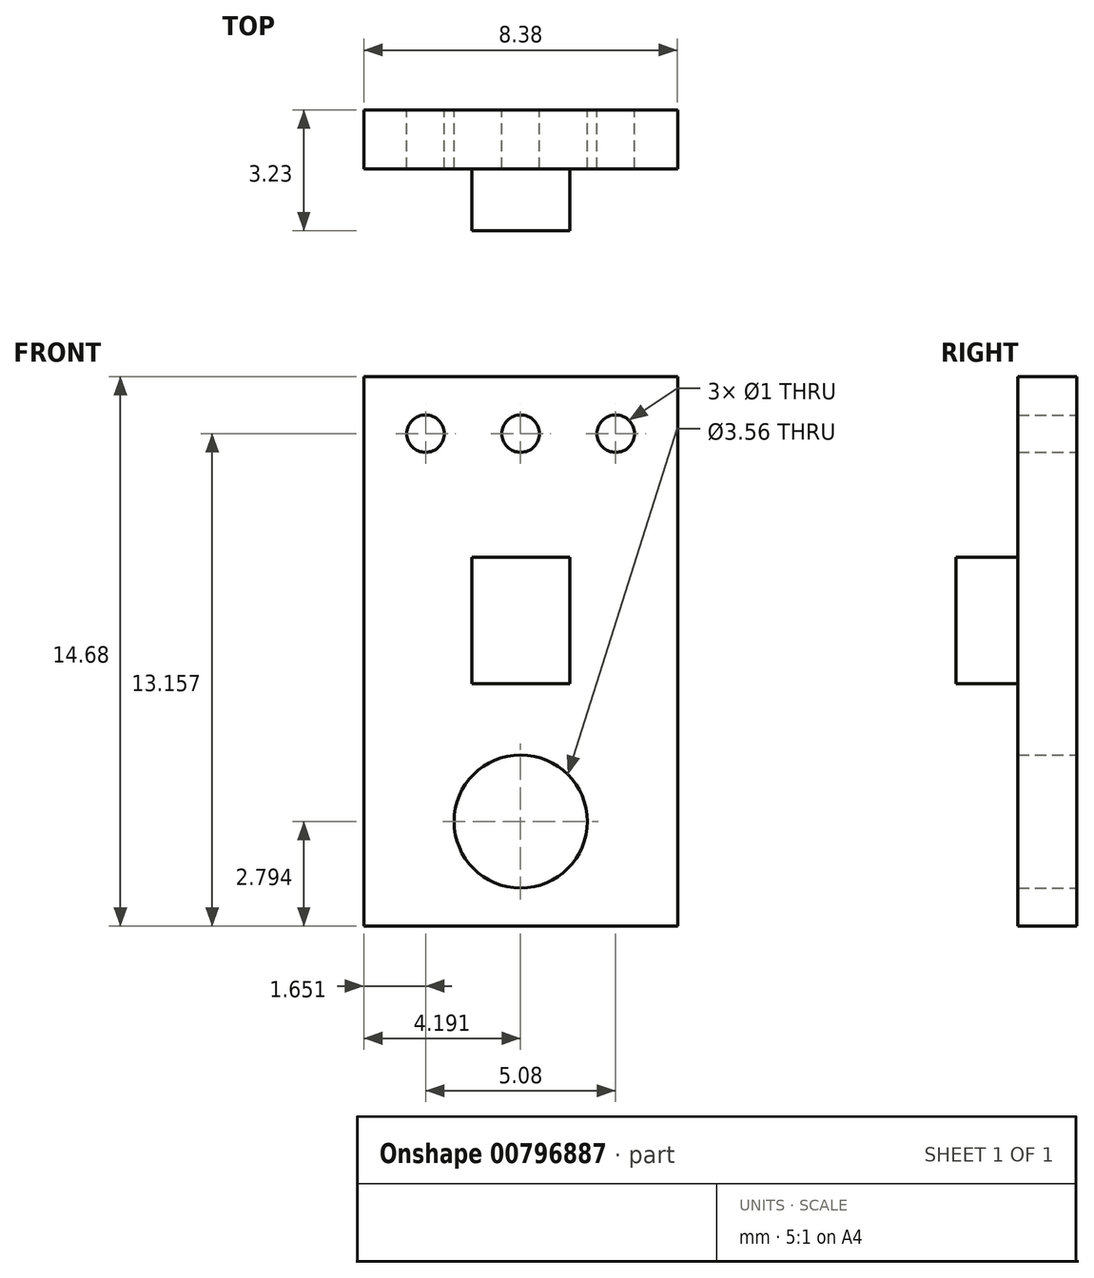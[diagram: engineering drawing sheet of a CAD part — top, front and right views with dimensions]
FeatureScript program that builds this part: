
annotation { "Feature Type Name" : "Feature", "Feature Type Description" : "" }
export const myFeature = defineFeature(function(context is Context, id is Id, definition is map)
    precondition{}
    {
        {
            var Q0;
            Q0=qCreatedBy(makeId("Front.planeOp"),FACE);
            var sketch = newSketch(context, id + "F0", { "sketchPlane" : qUnion([Q0])});
            skLineSegment(sketch, "E0.bottom", {"start": v(0, 0) * mm, "end": v(8.38, 0) * mm});
            skLineSegment(sketch, "E0.top", {"start": v(0, 14.68) * mm, "end": v(8.38, 14.68) * mm});
            skLineSegment(sketch, "E0.left", {"start": v(0, 0) * mm, "end": v(0, 14.68) * mm});
            skLineSegment(sketch, "E0.right", {"start": v(8.38, 0) * mm, "end": v(8.38, 14.68) * mm});
            skCircle(sketch, "E1", {"center": v(4.2, 2.8) * mm, "radius": 1.78 * mm});
            skCircle(sketch, "E2", {"center": v(4.2, 13.16) * mm, "radius": 0.5 * mm});
            skLineSegment(sketch, "E3", {"start": v(4.2, 14.68) * mm, "end": v(4.2, 0) * mm, "construction": true});
            skCircle(sketch, "E4.1.0.0", {"center": v(6.73, 13.16) * mm, "radius": 0.5 * mm});
            skLineSegment(sketch, "E4.direction1", {"start": v(4.2, 13.16) * mm, "end": v(6.73, 13.16) * mm, "construction": true});
            skCircle(sketch, "E5.1.0.0", {"center": v(1.65, 13.16) * mm, "radius": 0.5 * mm});
            skLineSegment(sketch, "E5.direction1", {"start": v(4.2, 13.16) * mm, "end": v(1.65, 13.16) * mm, "construction": true});
            skSolve(sketch);
        }
        {
            var Q0;
            Q0=makeQuery(id+"F0.imprint","IMPRINT",FACE,{"disambiguationData":[TD([[makeQuery(id+"F0.imprint","IMPRINT",EDGE,{"derivedFrom":sQuery(id+"F0.wireOp",EDGE,"E0.bottom")}),1.0]])]});
            extrude(context, id + "F1", {"entities" : qUnion([Q0]), "depth" : 1.57 * mm, "offsetDistance" : 25 * mm});
        }
        {
            var Q0;
            Q0=makeQuery(id+"F1.opExtrude","CAP_FACE",FACE,{"disambiguationData":[OSD([sQuery(id+"F0.wireOp",EDGE,"E0.bottom"),sQuery(id+"F0.wireOp",EDGE,"E0.top"),sQuery(id+"F0.wireOp",EDGE,"E0.left"),sQuery(id+"F0.wireOp",EDGE,"E0.right"),sQuery(id+"F0.wireOp",EDGE,"E1"),sQuery(id+"F0.wireOp",EDGE,"E2"),sQuery(id+"F0.wireOp",EDGE,"E4.1.0.0"),sQuery(id+"F0.wireOp",EDGE,"E5.1.0.0")])],"isStart":false});
            var sketch = newSketch(context, id + "F2", { "sketchPlane" : qUnion([Q0])});
            skLineSegment(sketch, "E6.bottom", {"start": v(2.88, 9.86) * mm, "end": v(5.5, 9.86) * mm});
            skLineSegment(sketch, "E6.top", {"start": v(2.88, 6.48) * mm, "end": v(5.5, 6.48) * mm});
            skLineSegment(sketch, "E6.left", {"start": v(2.88, 9.86) * mm, "end": v(2.88, 6.48) * mm});
            skLineSegment(sketch, "E6.right", {"start": v(5.5, 9.86) * mm, "end": v(5.5, 6.48) * mm});
            skLineSegment(sketch, "E7", {"start": v(4.2, 14.68) * mm, "end": v(4.2, 0) * mm, "construction": true});
            skSolve(sketch);
        }
        {
            var Q0;
            Q0=makeQuery(id+"F2.imprint","IMPRINT",FACE,{"disambiguationData":[TD([[makeQuery(id+"F2.imprint","IMPRINT",EDGE,{"derivedFrom":sQuery(id+"F2.wireOp",EDGE,"E6.bottom")}),-1.0]])]});
            extrude(context, id + "F3", {"entities" : qUnion([Q0]), "operationType" : NewBodyOperationType.ADD, "depth" : 1.65 * mm, "offsetDistance" : 25 * mm});
        }
    });
